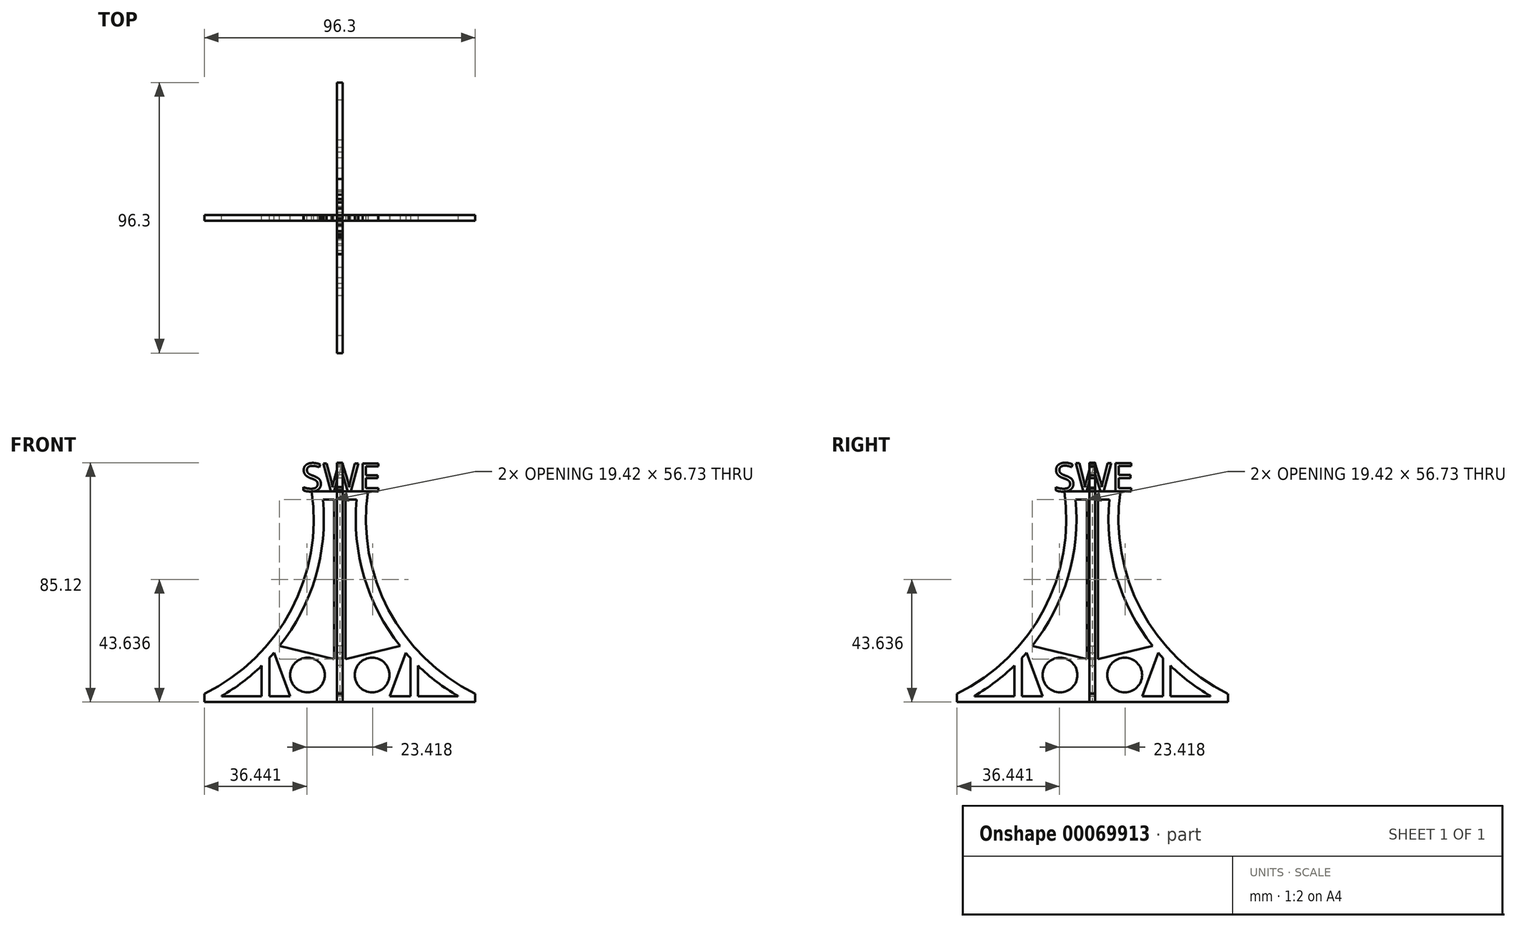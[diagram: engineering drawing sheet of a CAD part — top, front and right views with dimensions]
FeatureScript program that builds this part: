
annotation { "Feature Type Name" : "Feature", "Feature Type Description" : "" }
export const myFeature = defineFeature(function(context is Context, id is Id, definition is map)
    precondition{}
    {
        {
            var Q0;
            Q0=qCreatedBy(makeId("Right.planeOp"),FACE);
            var sketch = newSketch(context, id + "F0", { "sketchPlane" : qUnion([Q0])});
            skLineSegment(sketch, "E0", {"start": v(-10, 75) * mm, "end": v(0, 75) * mm});
            skLineSegment(sketch, "E1", {"start": v(0, 75) * mm, "end": v(0, 0) * mm});
            skLineSegment(sketch, "E2", {"start": v(0, 0) * mm, "end": v(-48.15, 0) * mm});
            skLineSegment(sketch, "E3", {"start": v(-48.15, 0) * mm, "end": v(-48.15, 3) * mm});
            skLineSegment(sketch, "E4", {"start": v(-2, 72) * mm, "end": v(-2, 2) * mm});
            skLineSegment(sketch, "E5", {"start": v(-2, 2) * mm, "end": v(-9.1, 2) * mm});
            skLineSegment(sketch, "E6", {"start": v(-2, 72) * mm, "end": v(-6, 72) * mm});
            skLineSegment(sketch, "E7", {"start": v(-42, 2) * mm, "end": v(-42, 2.18) * mm});
            skLineSegment(sketch, "E8.top", {"start": v(-25.08, 2) * mm, "end": v(-27.76, 2) * mm});
            skLineSegment(sketch, "E8.left", {"start": v(-25.08, 15.65) * mm, "end": v(-25.08, 2) * mm});
            skLineSegment(sketch, "E8.right", {"start": v(-27.76, 12.91) * mm, "end": v(-27.76, 2) * mm});
            skLineSegment(sketch, "E9.top", {"start": v(-12.03, 2) * mm, "end": v(-9.1, 2) * mm});
            skLineSegment(sketch, "E10.top", {"start": v(-17.72, 2) * mm, "end": v(-5.55, 2) * mm});
            skLineSegment(sketch, "E10.right", {"start": v(-23.43, 17.5) * mm, "end": v(-17.72, 2) * mm});
            skPoint(sketch, "E11.firstSnap0", {"position": v(-12, 15.27) * mm});
            skLineSegment(sketch, "E11.bottom", {"start": v(-21.42, 19.92) * mm, "end": v(-2, 15.27) * mm});
            skPoint(sketch, "E12.orphan", {"position": v(-2, 15.27) * mm});
            skLineSegment(sketch, "E13.trimOffspring", {"start": v(-12.03, 2) * mm, "end": v(-42, 2) * mm});
            skArc(sketch, "E14", {"start": v(-48.15, 3) * mm, "mid": v(-17.31, 32.77) * mm, "end": v(-10, 75) * mm});
            skArc(sketch, "E15", {"start": v(-42, 2.18) * mm, "mid": v(-34.55, 7.1) * mm, "end": v(-27.76, 12.91) * mm});
            skArc(sketch, "E16.trimOffspring", {"start": v(-21.42, 19.92) * mm, "mid": v(-8.65, 44.46) * mm, "end": v(-6, 72) * mm});
            skArc(sketch, "E17.trimOffspring", {"start": v(-25.08, 15.65) * mm, "mid": v(-24.25, 16.57) * mm, "end": v(-23.43, 17.5) * mm});
            skCircle(sketch, "E18", {"center": v(-11.5, 9.6) * mm, "radius": 6.18 * mm});
            skSolve(sketch);
        }
        {
            var Q0;
            Q0=qSketchRegion(id+"F0",true);
            extrude(context, id + "F1", {"entities" : qUnion([Q0]), "depth" : 1 * mm, "hasSecondDirection" : true, "secondDirectionOppositeDirection" : true, "secondDirectionDepth" : 1 * mm});
        }
        {
            var Q0;
            Q0=qCreatedBy(makeId("Right.planeOp"),FACE);
            var sketch = newSketch(context, id + "F2", { "sketchPlane" : qUnion([Q0])});
            skLineSegment(sketch, "E19", {"start": v(0, 81) * mm, "end": v(0, -28.5) * mm, "construction": true});
            skSolve(sketch);
        }
        {
            var Q0;
            Q0=makeQuery(id+"F1.opExtrude","SWEPT_BODY",BODY,{"disambiguationData":[OSD([sQuery(id+"F0.wireOp",EDGE,"E0"),sQuery(id+"F0.wireOp",EDGE,"E1"),sQuery(id+"F0.wireOp",EDGE,"E2"),sQuery(id+"F0.wireOp",EDGE,"E3"),sQuery(id+"F0.wireOp",EDGE,"ba3e6201-bb00-4176-be12-0bcf97df4df2"),sQuery(id+"F0.wireOp",EDGE,"E4"),sQuery(id+"F0.wireOp",EDGE,"E5"),sQuery(id+"F0.wireOp",EDGE,"E6"),sQuery(id+"F0.wireOp",EDGE,"E7"),sQuery(id+"F0.wireOp",EDGE,"973229ff-babc-457a-ac66-6eeaf75bea45")])]});
            var Q1;
            Q1=sQuery(id+"F2.wireOp",EDGE,"E19");
            circularPattern(context, id + "F3", {"entities" : qUnion([Q0]), "axis" : qUnion([Q1]), "angle" : 90 * degree, "instanceCount" : round(4)});
        }
        {
            var Q0;
            Q0=qCreatedBy(makeId("Front.planeOp"),FACE);
            var sketch = newSketch(context, id + "F4", { "sketchPlane" : qUnion([Q0])});
            skText(sketch, "E20", { "text": "SWE", "fontName": "OpenSans-Regular.ttf"});
            const initialGuessF4  = {"E20": [-0.01369, 0.075, 1, 0, 0.01]};
            skSetInitialGuess(sketch, initialGuessF4);
            skSolve(sketch);
        }
        {
            var Q0;
            Q0 = qSketchRegion(id + "F4", true);
            extrude(context, id + "F5", {"entities" : qUnion([Q0]), "depth" : 1 * mm, "hasSecondDirection" : true, "secondDirectionOppositeDirection" : true, "secondDirectionDepth" : 1 * mm});
        }
        {
            var Q0;
            Q0=qCreatedBy(makeId("Right.planeOp"),FACE);
            var sketch = newSketch(context, id + "F6", { "sketchPlane" : qUnion([Q0])});
            skText(sketch, "E21", { "text": "SWE", "fontName": "OpenSans-Regular.ttf"});
            const initialGuessF6  = {"E21": [-0.01376, 0.075, 1, 0, 0.01006]};
            skSetInitialGuess(sketch, initialGuessF6);
            skSolve(sketch);
        }
        {
            var Q0;
            Q0 = qSketchRegion(id + "F6", true);
            extrude(context, id + "F7", {"entities" : qUnion([Q0]), "depth" : 1 * mm, "hasSecondDirection" : true, "secondDirectionOppositeDirection" : true, "secondDirectionDepth" : 1 * mm});
        }
        {
            var Q0;
            Q0 = qSketchRegion(id + "F6", true);
            extrude(context, id + "F8", {"entities" : qUnion([Q0]), "depth" : 1 * mm, "hasSecondDirection" : true, "secondDirectionOppositeDirection" : true, "secondDirectionDepth" : 1 * mm});
        }
    });
